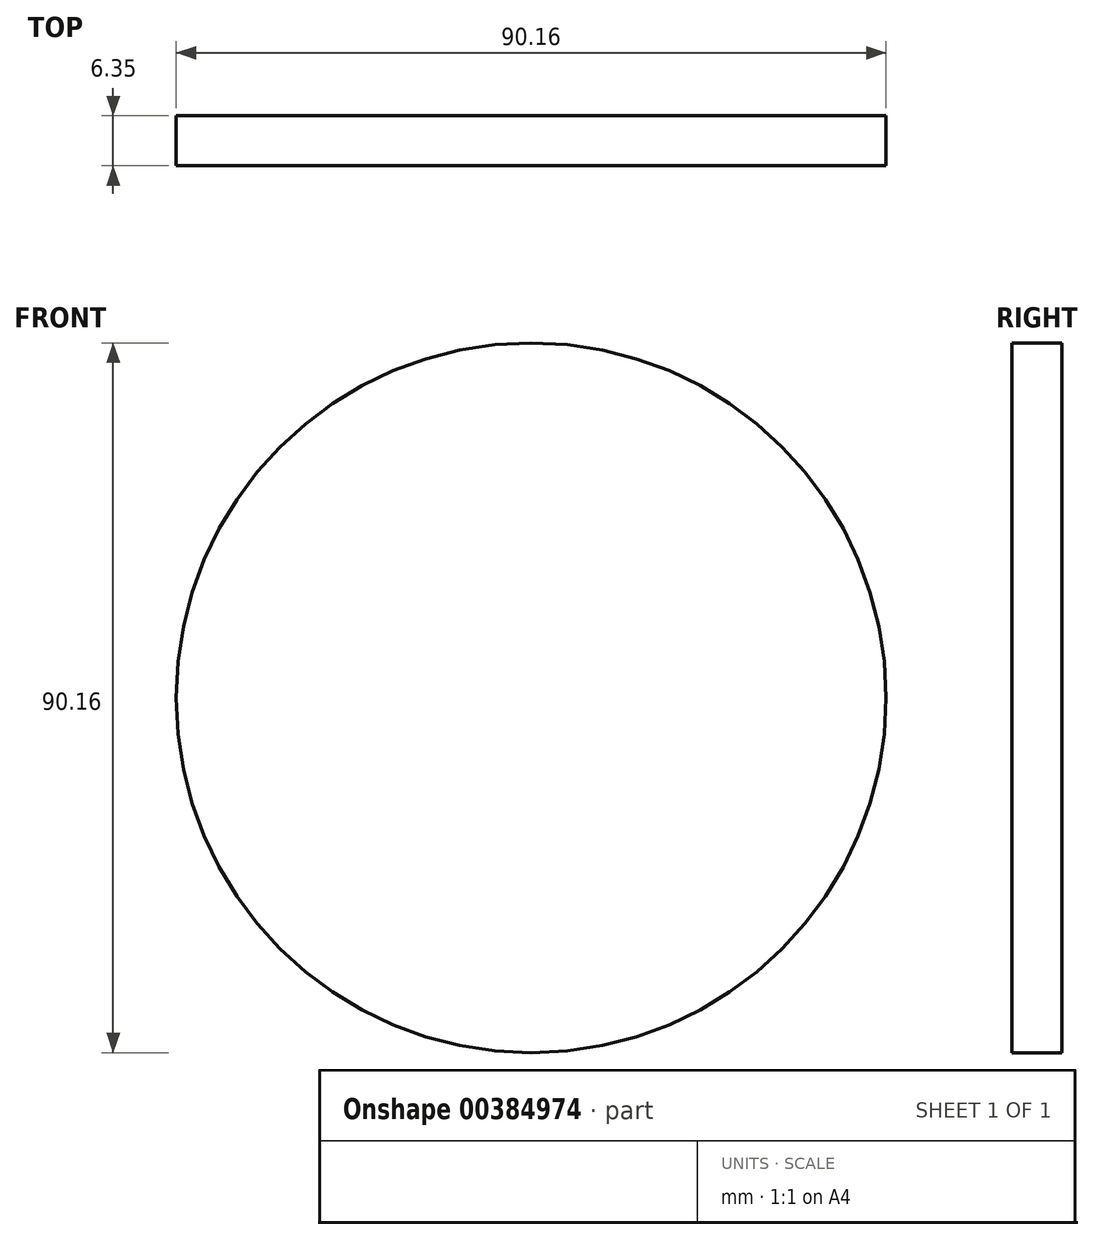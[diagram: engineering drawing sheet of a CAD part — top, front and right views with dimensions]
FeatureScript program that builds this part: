
annotation { "Feature Type Name" : "Feature", "Feature Type Description" : "" }
export const myFeature = defineFeature(function(context is Context, id is Id, definition is map)
    precondition{}
    {
        {
            var Q0;
            Q0=qCreatedBy(makeId("Front.planeOp"),FACE);
            var sketch = newSketch(context, id + "F0", { "sketchPlane" : qUnion([Q0])});
            skCircle(sketch, "E0", {"center": v(0, 0) * mm, "radius": 45.08 * mm});
            skSolve(sketch);
        }
        {
            var Q0;
            Q0=makeQuery(id+"F0.imprint","IMPRINT",FACE,{"disambiguationData":[TD([[makeQuery(id+"F0.imprint","IMPRINT",EDGE,{"derivedFrom":sQuery(id+"F0.wireOp",EDGE,"E0")}),1.0]])]});
            extrude(context, id + "F1", {"entities" : qUnion([Q0]), "depth" : 6.35 * mm});
        }
    });
